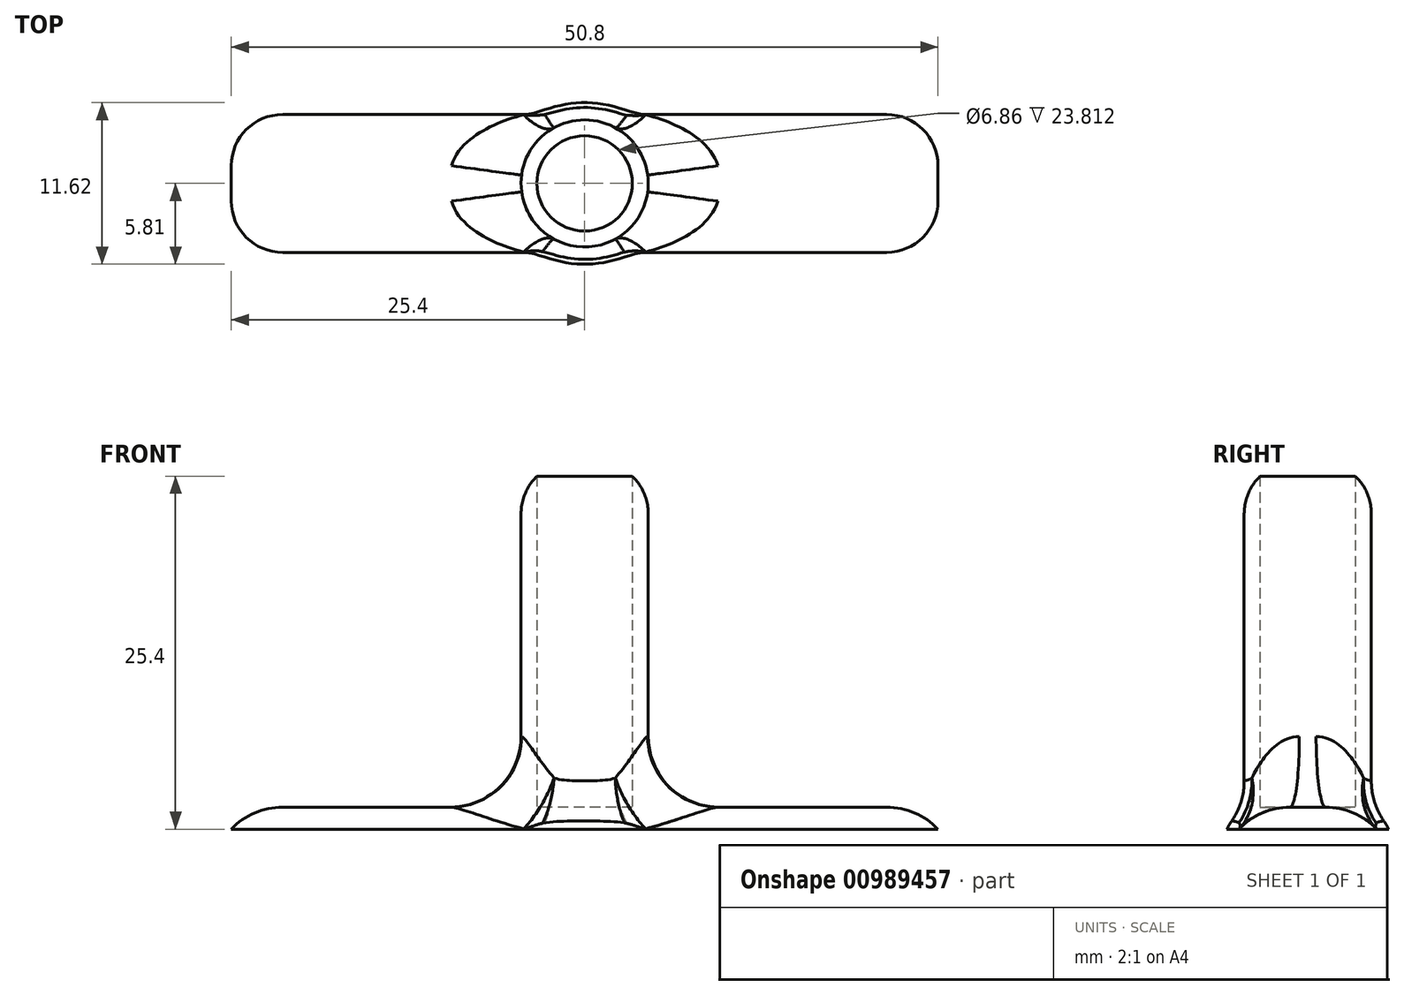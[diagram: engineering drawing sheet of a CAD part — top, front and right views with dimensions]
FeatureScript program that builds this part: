
annotation { "Feature Type Name" : "Feature", "Feature Type Description" : "" }
export const myFeature = defineFeature(function(context is Context, id is Id, definition is map)
    precondition{}
    {
        {
            var Q0;
            Q0=qCreatedBy(makeId("Top.planeOp"),FACE);
            var sketch = newSketch(context, id + "F0", { "sketchPlane" : qUnion([Q0])});
            skLineSegment(sketch, "E0.bottom", {"start": v(25.4, 6.35) * mm, "end": v(-25.4, 6.35) * mm});
            skLineSegment(sketch, "E0.top", {"start": v(25.4, -6.35) * mm, "end": v(-25.4, -6.35) * mm});
            skLineSegment(sketch, "E0.left", {"start": v(25.4, 6.35) * mm, "end": v(25.4, -6.35) * mm});
            skLineSegment(sketch, "E0.right", {"start": v(-25.4, 6.35) * mm, "end": v(-25.4, -6.35) * mm});
            skPoint(sketch, "E0.middle", {"position": v(0, 0) * mm});
            skCircle(sketch, "E1", {"center": v(0, 0) * mm, "radius": 3.43 * mm});
            skCircle(sketch, "E2", {"center": v(0, 0) * mm, "radius": 4.57 * mm});
            skSolve(sketch);
        }
        {
            var Q0;
            Q0=makeQuery(id+"F0.imprint","IMPRINT",FACE,{"disambiguationData":[TD([[makeQuery(id+"F0.imprint","IMPRINT",EDGE,{"derivedFrom":sQuery(id+"F0.wireOp",EDGE,"E0.bottom")}),1.0]])]});
            var Q1;
            Q1=makeQuery(id+"F0.imprint","IMPRINT",FACE,{"disambiguationData":[TD([[makeQuery(id+"F0.imprint","IMPRINT",EDGE,{"derivedFrom":sQuery(id+"F0.wireOp",EDGE,"E1")}),1.0]])]});
            var Q2;
            Q2=makeQuery(id+"F0.imprint","IMPRINT",FACE,{"disambiguationData":[TD([[makeQuery(id+"F0.imprint","IMPRINT",EDGE,{"derivedFrom":sQuery(id+"F0.wireOp",EDGE,"E1")}),-1.0]])]});
            extrude(context, id + "F1", {"entities" : qUnion([Q0, Q1, Q2]), "depth" : 1.59 * mm, "offsetDistance" : 25.4 * mm});
        }
        {
            var Q0;
            Q0=makeQuery(id+"F1.opExtrude","CAP_EDGE",EDGE,{"disambiguationData":[OSD([sQuery(id+"F0.wireOp",EDGE,"E0.right")])],"isStart":false});
            var Q1;
            Q1=makeQuery(id+"F1.opExtrude","CAP_EDGE",EDGE,{"disambiguationData":[OSD([sQuery(id+"F0.wireOp",EDGE,"E0.left")])],"isStart":false});
            fillet(context, id + "F2", {"entities" : qUnion([Q0, Q1]), "radius" : 5.08 * mm, "tangentPropagation" : true, "allowEdgeOverflow" : false});
        }
        {
            var Q0;
            Q0=makeQuery(id+"F0.imprint","IMPRINT",FACE,{"disambiguationData":[TD([[makeQuery(id+"F0.imprint","IMPRINT",EDGE,{"derivedFrom":sQuery(id+"F0.wireOp",EDGE,"E1")}),-1.0]])]});
            extrude(context, id + "F3", {"entities" : qUnion([Q0]), "operationType" : NewBodyOperationType.ADD, "depth" : 25.4 * mm, "offsetDistance" : 25.4 * mm});
        }
        {
            var Q0;
            Q0=makeQuery(id+"F1.opExtrude","CAP_EDGE",EDGE,{"disambiguationData":[OSD([sQuery(id+"F0.wireOp",EDGE,"E0.top")])],"isStart":false});
            var Q1;
            Q1=makeQuery(id+"F1.opExtrude","CAP_EDGE",EDGE,{"disambiguationData":[OSD([sQuery(id+"F0.wireOp",EDGE,"E0.bottom")])],"isStart":false});
            fillet(context, id + "F4", {"entities" : qUnion([Q0, Q1]), "radius" : 5.08 * mm, "tangentPropagation" : true, "allowEdgeOverflow" : false});
        }
        {
            var Q0;
            Q0=makeQuery(id+"F4.opFillet","BLEND_EDGE",EDGE,{"blendedFrom":[makeQuery(id+"F1.opExtrude","CAP_EDGE",EDGE,{"disambiguationData":[OSD([sQuery(id+"F0.wireOp",EDGE,"E0.top")])],"isStart":false}),makeQuery(id+"F3.opExtrude","SWEPT_FACE",FACE,{"disambiguationData":[OSD([sQuery(id+"F0.wireOp",EDGE,"E2")])]})],"blendedInto":[makeQuery(id+"F3.opExtrude","SWEPT_FACE",FACE,{"disambiguationData":[OSD([sQuery(id+"F0.wireOp",EDGE,"E2")])]})]});
            var Q1;
            Q1=makeQuery(id+"F3.boolean.opBoolean","INTERSECT",EDGE,{"derivedFrom":[makeQuery(id+"F1.opExtrude","CAP_FACE",FACE,{"disambiguationData":[OSD([sQuery(id+"F0.wireOp",EDGE,"E0.bottom"),sQuery(id+"F0.wireOp",EDGE,"E0.top"),sQuery(id+"F0.wireOp",EDGE,"E0.left"),sQuery(id+"F0.wireOp",EDGE,"E0.right")])],"isStart":false}),makeQuery(id+"F3.opExtrude","SWEPT_FACE",FACE,{"disambiguationData":[OSD([sQuery(id+"F0.wireOp",EDGE,"E2")])]})]});
            var Q2;
            Q2=makeQuery(id+"F4.opFillet","BLEND_EDGE",EDGE,{"blendedFrom":[makeQuery(id+"F1.opExtrude","CAP_EDGE",EDGE,{"disambiguationData":[OSD([sQuery(id+"F0.wireOp",EDGE,"E0.bottom")])],"isStart":false}),makeQuery(id+"F3.opExtrude","SWEPT_FACE",FACE,{"disambiguationData":[OSD([sQuery(id+"F0.wireOp",EDGE,"E2")])]})],"blendedInto":[makeQuery(id+"F3.opExtrude","SWEPT_FACE",FACE,{"disambiguationData":[OSD([sQuery(id+"F0.wireOp",EDGE,"E2")])]})]});
            fillet(context, id + "F5", {"entities" : qUnion([Q0, Q1, Q2]), "radius" : 5.08 * mm, "tangentPropagation" : true, "allowEdgeOverflow" : false});
        }
        {
            var Q0;
            Q0=makeQuery(id+"F3.opExtrude","CAP_EDGE",EDGE,{"disambiguationData":[OSD([sQuery(id+"F0.wireOp",EDGE,"E2")])],"isStart":false});
            fillet(context, id + "F6", {"entities" : qUnion([Q0]), "radius" : 3.8 * mm, "tangentPropagation" : true, "allowEdgeOverflow" : false});
        }
    });
